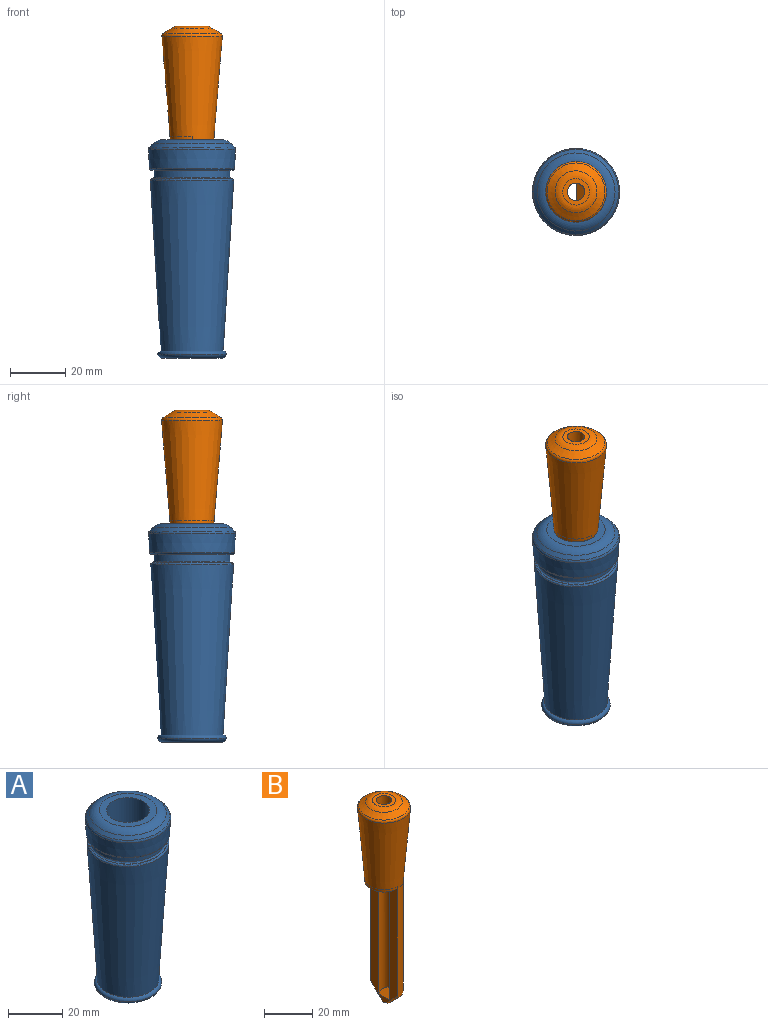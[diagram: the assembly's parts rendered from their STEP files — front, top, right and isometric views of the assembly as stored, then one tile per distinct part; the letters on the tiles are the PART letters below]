
ASSEMBLY  parts=2 mates=1
PART A: 17 faces, bbox 34.3x34.3x79.4 mm
  f0: plane 21.19x21.19mm, normal (0,0,1), area 154.8mm2, adj f8,f9
  f1: cone r=12.7mm half-angle=45deg, axis (0,0,-1), area 169mm2, adj f9,f10
  f2: cone r=15.88mm half-angle=3.5deg, axis (0,0,1), area 666.2mm2, adj f10,f11
  f3: plane 29.58x29.58mm, normal (0,0,-1), area 88.9mm2, adj f4,f11
  f4: cylinder r=13.8mm len=27.6mm, axis (0,0,1), area 220.2mm2, adj f3,f13
  f5: plane 29.03x29.03mm, normal (0,0,1), area 7.4mm2, adj f12,f13
  f6: cone r=15.19mm half-angle=3.5deg, axis (0,0,1), area 5157.1mm2, adj f12,f14
  f7: plane 21.88x21.88mm, normal (0,0,-1), area 152mm2, adj f15,f16
  f8: cylinder r=7.94mm len=78.87mm, axis (0,0,1), area 3933.3mm2, adj f0,f16
  f9: torus R=10.6mm, axis (0,0,1), area 313.1mm2, adj f0,f1
  f10: torus R=14.57mm, axis (0,0,-1), area 106.3mm2, adj f1,f2
  f11: torus R=14.79mm, axis (0,0,-1), area 91.4mm2, adj f2,f3
  f12: torus R=14.51mm, axis (0,0,-1), area 97.2mm2, adj f5,f6
  f13: torus R=14.43mm, axis (0,0,-1), area 87.9mm2, adj f4,f5
  f14: torus R=11.18mm, axis (0,0,1), area 139.1mm2, adj f6,f15
  f15: torus R=10.94mm, axis (0,0,-1), area 160mm2, adj f7,f14
  f16: torus R=8.45mm, axis (0,0,1), area 40.7mm2, adj f7,f8
PART B: 13 faces, bbox 25.3x25.3x105.1 mm
  f0: plane 63.26x15.88mm, normal (-1,0,0), area 568.3mm2, adj f1,f3,f6,f10,f11,f12
  f1: cylinder r=7.94mm len=15.88mm, axis (0,0,-1), area 31.7mm2, adj f0,f2,f12
  f2: cone r=7.94mm half-angle=4.8deg, axis (0,0,1), area 2235.9mm2, adj f1,f3,f8
  f3: cylinder r=7.94mm len=55.88mm, axis (0,0,-1), area 1392.5mm2, adj f0,f2,f9,f10
  f4: plane 9.62x9.62mm, normal (0,0,1), area 41.1mm2, adj f6,f7
  f5: cone r=11.11mm half-angle=56.3deg, axis (0,0,-1), area 195.6mm2, adj f7,f8
  f6: cylinder r=3.17mm len=100.33mm, axis (0,0,1), area 1383.9mm2, adj f0,f4,f11,f12
  f7: torus R=4.81mm, axis (0,0,-1), area 117.5mm2, adj f4,f5
  f8: torus R=9.78mm, axis (0,0,1), area 92.5mm2, adj f2,f5
  f9: cone r=0.32mm half-angle=45deg, axis (0,0,1), area 118.4mm2, adj f3,f10
  f10: bspline ~18.48x8.54mm, area 25.1mm2, adj f0,f3,f9
  f11: plane 7.69x4.51mm, normal (-0.71,0,0.71), area 22.4mm2, adj f0,f6
  f12: plane 15.88x7.94mm, normal (0,0,-1), area 83.1mm2, adj f0,f1,f6
PLACE A t=(0,0,-63.5)mm
PLACE B t=(-43.14,0,-63.5)mm
MATE revolute B.f1 <-> A.f8  axis (0,0,-1) through (-29.29,0,-63.5)mm
